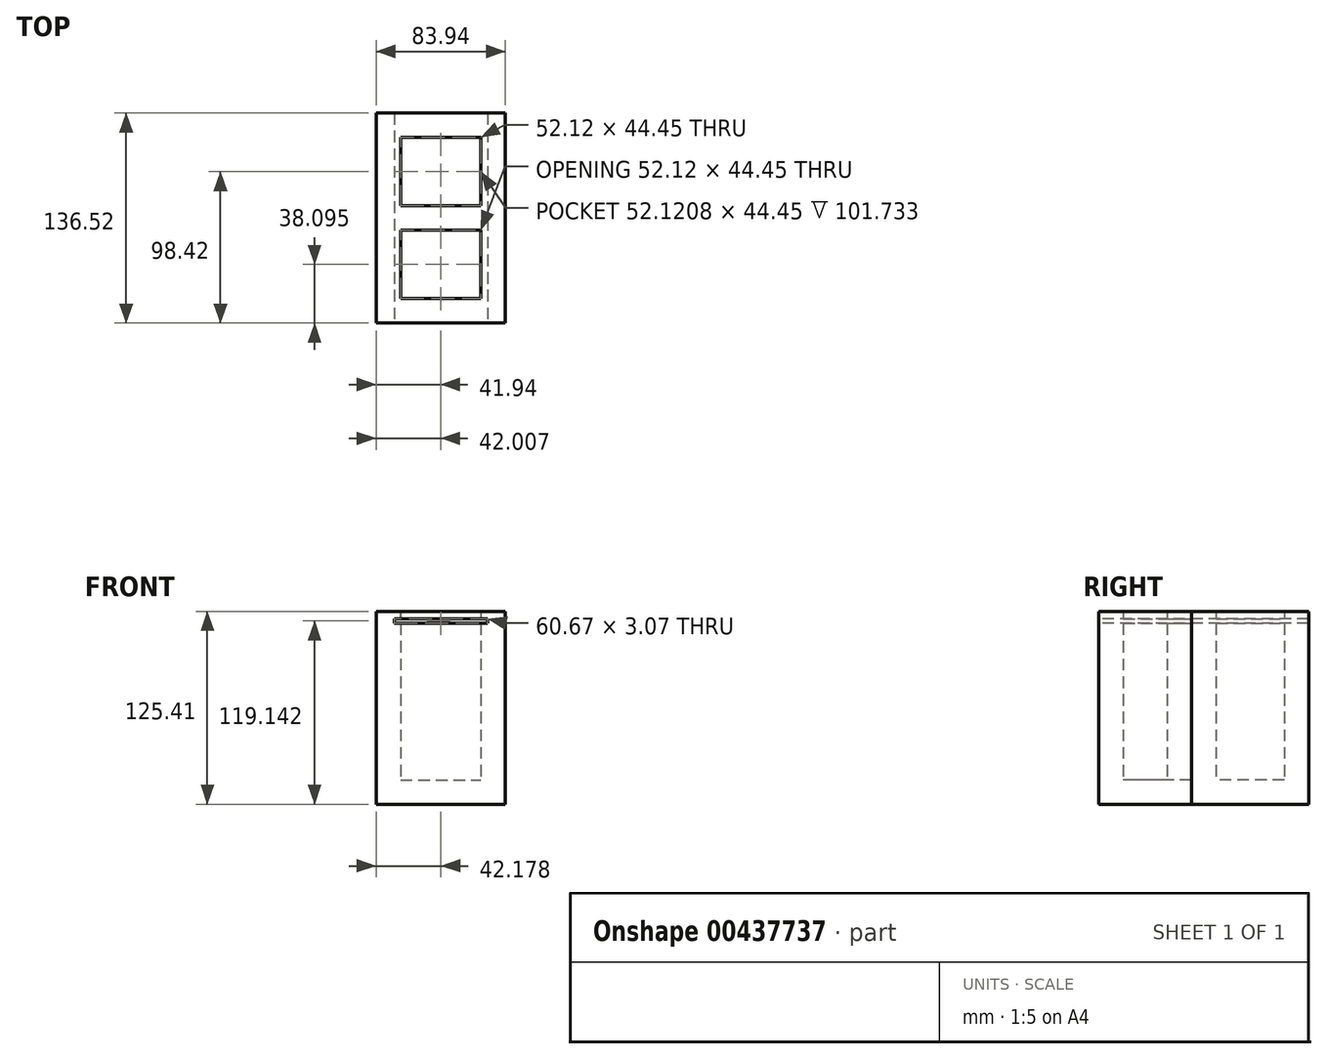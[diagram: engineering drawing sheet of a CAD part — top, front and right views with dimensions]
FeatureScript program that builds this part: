
annotation { "Feature Type Name" : "Feature", "Feature Type Description" : "" }
export const myFeature = defineFeature(function(context is Context, id is Id, definition is map)
    precondition{}
    {
        {
            var Q0;
            Q0=qCreatedBy(makeId("Top.planeOp"),FACE);
            var sketch = newSketch(context, id + "F0", { "sketchPlane" : qUnion([Q0])});
            skLineSegment(sketch, "E0.bottom", {"start": v(-41.94, 38.1) * mm, "end": v(41.94, 38.1) * mm});
            skLineSegment(sketch, "E0.top", {"start": v(-41.94, -38.1) * mm, "end": v(41.94, -38.1) * mm});
            skLineSegment(sketch, "E0.left", {"start": v(-41.94, 38.1) * mm, "end": v(-41.94, -38.1) * mm});
            skLineSegment(sketch, "E0.right", {"start": v(41.94, 38.1) * mm, "end": v(41.94, -38.1) * mm});
            skLineSegment(sketch, "E1", {"start": v(41.94, 38.1) * mm, "end": v(-41.94, -38.1) * mm});
            skSolve(sketch);
        }
        {
            var Q0;
            Q0 = qSketchRegion(id + "F0", true);
            extrude(context, id + "F1", {"entities" : qUnion([Q0]), "depth" : 125.4 * mm});
        }
        {
            var Q0;
            Q0=makeQuery(id+"F1.opExtrude","CAP_FACE",FACE,{"disambiguationData":[OSD([sQuery(id+"F0.wireOp",EDGE,"E0.bottom"),sQuery(id+"F0.wireOp",EDGE,"E0.top"),sQuery(id+"F0.wireOp",EDGE,"E0.left"),sQuery(id+"F0.wireOp",EDGE,"E0.right")])],"isStart":false});
            shell(context, id + "F2", {"entities" : qUnion([Q0]), "thickness" : 15.88 * mm});
        }
        {
            var Q0;
            Q0=qCreatedBy(makeId("Top.planeOp"),FACE);
            var sketch = newSketch(context, id + "F3", { "sketchPlane" : qUnion([Q0])});
            skLineSegment(sketch, "E2.bottom", {"start": v(-41.87, -38.1) * mm, "end": v(42, -38.1) * mm});
            skLineSegment(sketch, "E2.top", {"start": v(-41.87, -98.43) * mm, "end": v(42, -98.43) * mm});
            skLineSegment(sketch, "E2.left", {"start": v(-41.87, -38.1) * mm, "end": v(-41.87, -98.43) * mm});
            skLineSegment(sketch, "E2.right", {"start": v(42, -38.1) * mm, "end": v(42, -98.43) * mm});
            skLineSegment(sketch, "E3", {"start": v(42, -98.43) * mm, "end": v(-41.87, -38.1) * mm});
            skSolve(sketch);
        }
        {
            var Q0;
            Q0 = qSketchRegion(id + "F3", true);
            extrude(context, id + "F4", {"entities" : qUnion([Q0]), "operationType" : NewBodyOperationType.ADD, "depth" : 125.4 * mm});
        }
        {
            var Q0;
            Q0=makeQuery(id+"F4.opExtrude","CAP_FACE",FACE,{"disambiguationData":[OSD([sQuery(id+"F3.wireOp",EDGE,"E2.bottom"),sQuery(id+"F3.wireOp",EDGE,"E2.top"),sQuery(id+"F3.wireOp",EDGE,"E2.left"),sQuery(id+"F3.wireOp",EDGE,"E2.right")])],"isStart":false});
            var Q1;
            Q1=makeQuery(id+"F1.opExtrude","SWEPT_BODY",BODY,{"disambiguationData":[OSD([sQuery(id+"F0.wireOp",EDGE,"E0.bottom"),sQuery(id+"F0.wireOp",EDGE,"E0.top"),sQuery(id+"F0.wireOp",EDGE,"E0.left"),sQuery(id+"F0.wireOp",EDGE,"E0.right")])]});
            shell(context, id + "F5", {"entities" : qUnion([Q0]), "parts" : qUnion([Q1]), "thickness" : 15.88 * mm});
        }
        {
            var Q0;
            Q0=makeQuery(id+"F4.opExtrude","SWEPT_FACE",FACE,{"disambiguationData":[OSD([sQuery(id+"F3.wireOp",EDGE,"E2.top")])]});
            cPlane(context, id + "F6", {"entities" : qUnion([Q0]), "cplaneType" : CPlaneType.OFFSET, "offset" : 25.4 * mm, "width" : 152.4 * mm, "height" : 152.4 * mm});
        }
        {
            var Q0;
            Q0=qCreatedBy(id+"F6.planeOp",FACE);
            var sketch = newSketch(context, id + "F7", { "sketchPlane" : qUnion([Q0])});
            skLineSegment(sketch, "E4.bottom", {"start": v(-30.1, 120.68) * mm, "end": v(30.57, 120.68) * mm});
            skLineSegment(sketch, "E4.top", {"start": v(-30.1, 117.6) * mm, "end": v(30.57, 117.6) * mm});
            skLineSegment(sketch, "E4.left", {"start": v(-30.1, 120.68) * mm, "end": v(-30.1, 117.6) * mm});
            skLineSegment(sketch, "E4.right", {"start": v(30.57, 120.68) * mm, "end": v(30.57, 117.6) * mm});
            skSolve(sketch);
        }
        {
            var Q0;
            Q0 = qSketchRegion(id + "F7", true);
            extrude(context, id + "F8", {"entities" : qUnion([Q0]), "operationType" : NewBodyOperationType.REMOVE, "oppositeDirection" : true, "depth" : 182.63 * mm, "hasSecondDirection" : true, "secondDirectionOppositeDirection" : false, "secondDirectionDepth" : 25.4 * mm});
        }
    });
